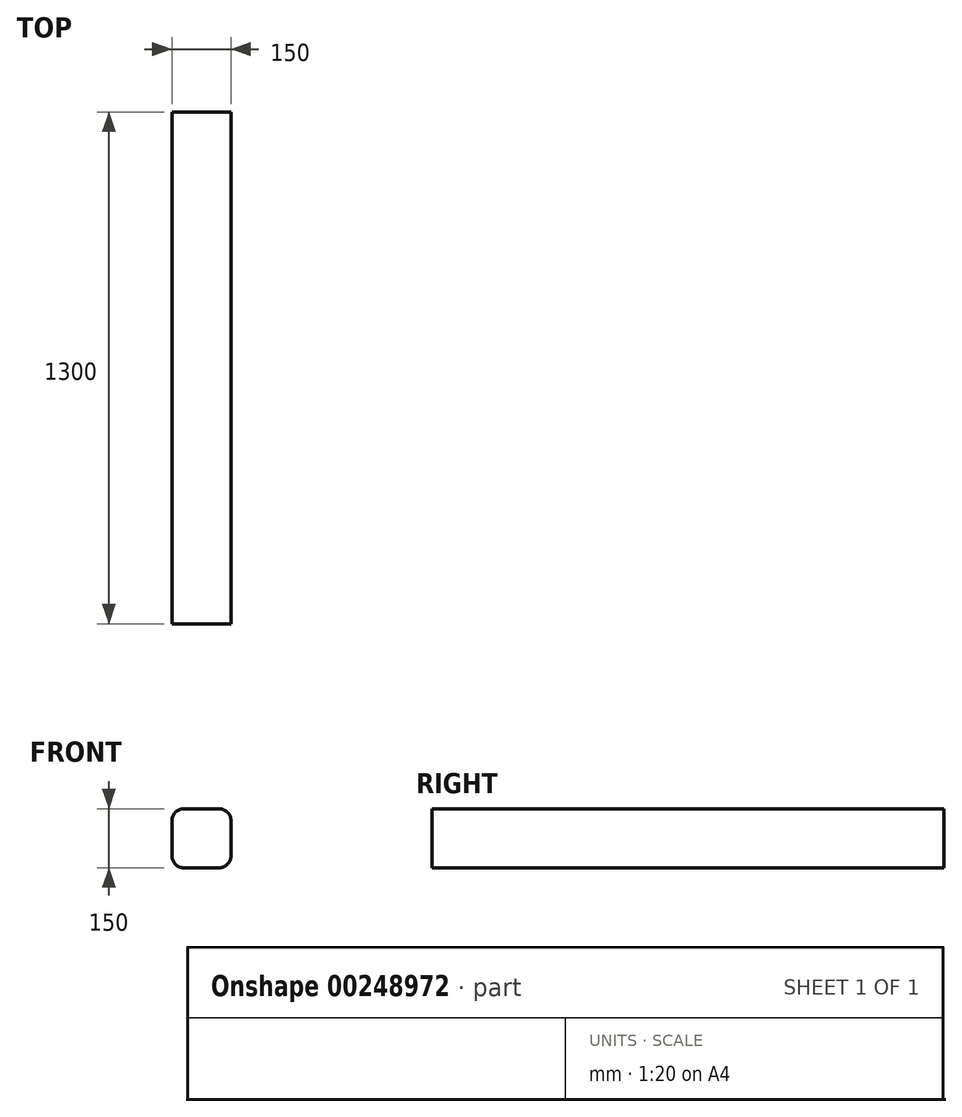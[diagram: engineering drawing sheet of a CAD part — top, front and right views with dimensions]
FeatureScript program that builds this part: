
annotation { "Feature Type Name" : "Feature", "Feature Type Description" : "" }
export const myFeature = defineFeature(function(context is Context, id is Id, definition is map)
    precondition{}
    {
        {
            var Q0;
            Q0=qCreatedBy(makeId("Front.planeOp"),FACE);
            var sketch = newSketch(context, id + "F0", { "sketchPlane" : qUnion([Q0])});
            skLineSegment(sketch, "E0.bottom", {"start": v(45, 75) * mm, "end": v(-45, 75) * mm});
            skLineSegment(sketch, "E0.top", {"start": v(45, -75) * mm, "end": v(-45, -75) * mm});
            skLineSegment(sketch, "E0.left", {"start": v(75, 45) * mm, "end": v(75, -45) * mm});
            skLineSegment(sketch, "E0.right", {"start": v(-75, 45) * mm, "end": v(-75, -45) * mm});
            skPoint(sketch, "E0.middle", {"position": v(0, 0) * mm});
            skPoint(sketch, "E1.visualSharp", {"position": v(75, 75) * mm});
            skArc(sketch, "E1.filletArc", {"start": v(75, 45) * mm, "mid": v(66.21, 66.21) * mm, "end": v(45, 75) * mm});
            skPoint(sketch, "E2.visualSharp", {"position": v(75, -75) * mm});
            skArc(sketch, "E2.filletArc", {"start": v(45, -75) * mm, "mid": v(66.21, -66.21) * mm, "end": v(75, -45) * mm});
            skPoint(sketch, "E3.visualSharp", {"position": v(-75, -75) * mm});
            skArc(sketch, "E3.filletArc", {"start": v(-75, -45) * mm, "mid": v(-66.21, -66.21) * mm, "end": v(-45, -75) * mm});
            skPoint(sketch, "E4.visualSharp", {"position": v(-75, 75) * mm});
            skArc(sketch, "E4.filletArc", {"start": v(-45, 75) * mm, "mid": v(-66.21, 66.21) * mm, "end": v(-75, 45) * mm});
            skSolve(sketch);
        }
        {
            var Q0;
            Q0 = qSketchRegion(id + "F0", true);
            extrude(context, id + "F1", {"entities" : qUnion([Q0]), "depth" : 1300 * mm});
        }
    });
